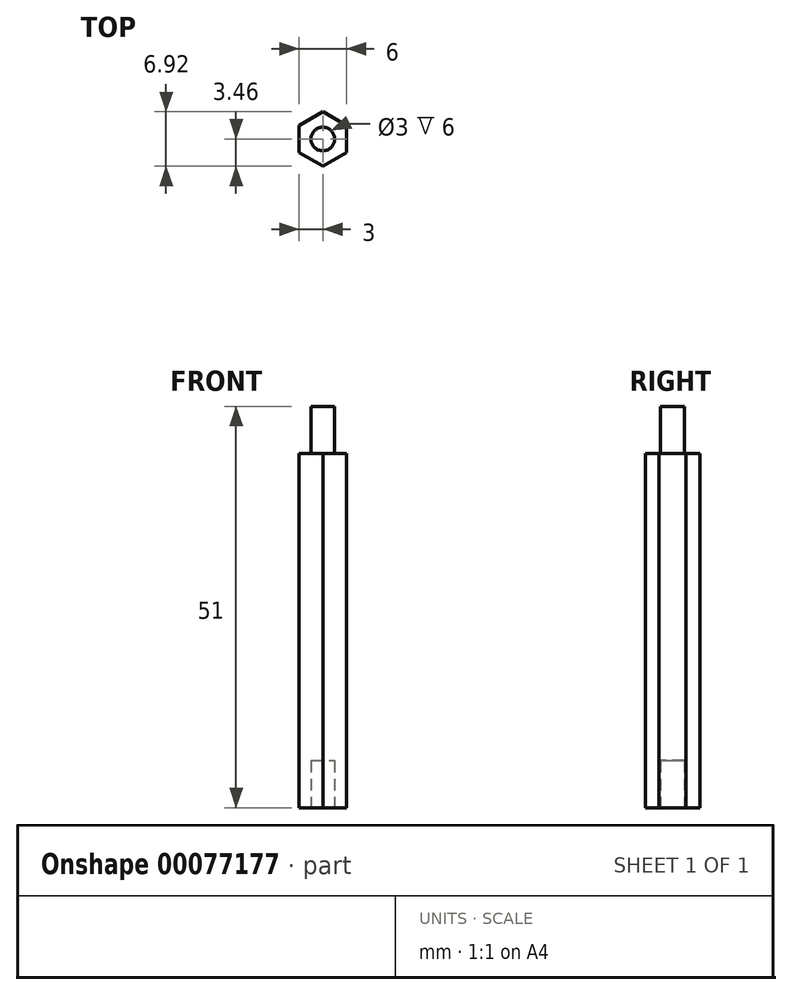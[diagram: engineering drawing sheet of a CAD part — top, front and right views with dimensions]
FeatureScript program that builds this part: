
annotation { "Feature Type Name" : "Feature", "Feature Type Description" : "" }
export const myFeature = defineFeature(function(context is Context, id is Id, definition is map)
    precondition{}
    {
        {
            var Q0;
            Q0=qCreatedBy(makeId("Top.planeOp"),FACE);
            var sketch = newSketch(context, id + "F0", { "sketchPlane" : qUnion([Q0])});
            skCircle(sketch, "E0.cCircle", {"center": v(0, 0) * mm, "radius": 3 * mm, "construction": true});
            skLineSegment(sketch, "E0.0", {"start": v(3, 1.73) * mm, "end": v(3, -1.73) * mm});
            skLineSegment(sketch, "E0.1", {"start": v(3, -1.73) * mm, "end": v(0, -3.46) * mm});
            skLineSegment(sketch, "E0.2", {"start": v(0, -3.46) * mm, "end": v(-3, -1.73) * mm});
            skLineSegment(sketch, "E0.3", {"start": v(-3, -1.73) * mm, "end": v(-3, 1.73) * mm});
            skLineSegment(sketch, "E0.4", {"start": v(-3, 1.73) * mm, "end": v(0, 3.46) * mm});
            skLineSegment(sketch, "E0.5", {"start": v(0, 3.46) * mm, "end": v(3, 1.73) * mm});
            skPoint(sketch, "E0.0.midPoint", {"position": v(3, 0) * mm});
            skSolve(sketch);
        }
        {
            var Q0;
            Q0=qSketchRegion(id+"F0",true);
            extrude(context, id + "F1", {"entities" : qUnion([Q0]), "depth" : 45 * mm});
        }
        {
            var Q0;
            Q0=makeQuery(id+"F1.opExtrude","CAP_FACE",FACE,{"disambiguationData":[OSD([sQuery(id+"F0.wireOp",EDGE,"E0.0"),sQuery(id+"F0.wireOp",EDGE,"E0.1"),sQuery(id+"F0.wireOp",EDGE,"E0.2"),sQuery(id+"F0.wireOp",EDGE,"E0.3"),sQuery(id+"F0.wireOp",EDGE,"E0.4"),sQuery(id+"F0.wireOp",EDGE,"E0.5")])],"isStart":false});
            var sketch = newSketch(context, id + "F2", { "sketchPlane" : qUnion([Q0])});
            skCircle(sketch, "E1", {"center": v(0, 0) * mm, "radius": 1.5 * mm});
            skSolve(sketch);
        }
        {
            var Q0;
            Q0=qSketchRegion(id+"F2",true);
            extrude(context, id + "F3", {"entities" : qUnion([Q0]), "operationType" : NewBodyOperationType.ADD, "depth" : 6 * mm});
        }
        {
            var Q0;
            Q0=makeQuery(id+"F1.opExtrude","CAP_FACE",FACE,{"disambiguationData":[OSD([sQuery(id+"F0.wireOp",EDGE,"E0.0"),sQuery(id+"F0.wireOp",EDGE,"E0.1"),sQuery(id+"F0.wireOp",EDGE,"E0.2"),sQuery(id+"F0.wireOp",EDGE,"E0.3"),sQuery(id+"F0.wireOp",EDGE,"E0.4"),sQuery(id+"F0.wireOp",EDGE,"E0.5")])],"isStart":true});
            var sketch = newSketch(context, id + "F4", { "sketchPlane" : qUnion([Q0])});
            skCircle(sketch, "E2", {"center": v(0, 0) * mm, "radius": 1.5 * mm});
            skSolve(sketch);
        }
        {
            var Q0;
            Q0=makeQuery(id+"F4.imprint","IMPRINT",FACE,{"disambiguationData":[TD([[makeQuery(id+"F4.imprint","IMPRINT",EDGE,{"derivedFrom":sQuery(id+"F4.wireOp",EDGE,"E2")}),1.0]])]});
            extrude(context, id + "F5", {"entities" : qUnion([Q0]), "operationType" : NewBodyOperationType.REMOVE, "oppositeDirection" : true, "depth" : 6 * mm});
        }
    });
